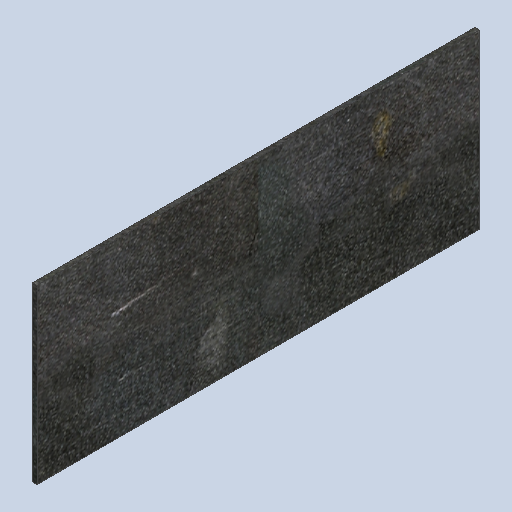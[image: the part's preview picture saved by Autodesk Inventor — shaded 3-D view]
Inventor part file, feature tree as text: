
AUTODESK INVENTOR PART (.ipt)
format: ipt  version: 2024.3 (Build 283343000, 343)  size: 274,944 bytes
history: native  units: mm
features: sheet_metal_op x1, sketch x1, other x1
ambient origin geometry x8: Origin, YZ Plane, XZ Plane, XY Plane, X Axis, Y Axis, Z Axis, Center Point
bodies: Solid1 (feature_tree)
feature tree (3):
  sheet_metal_op  "Face1"
  sketch  "Sketch1"  dims[d0=200.0mm d5=2.0mm d6=78.0mm]
  other  "Plate1"
